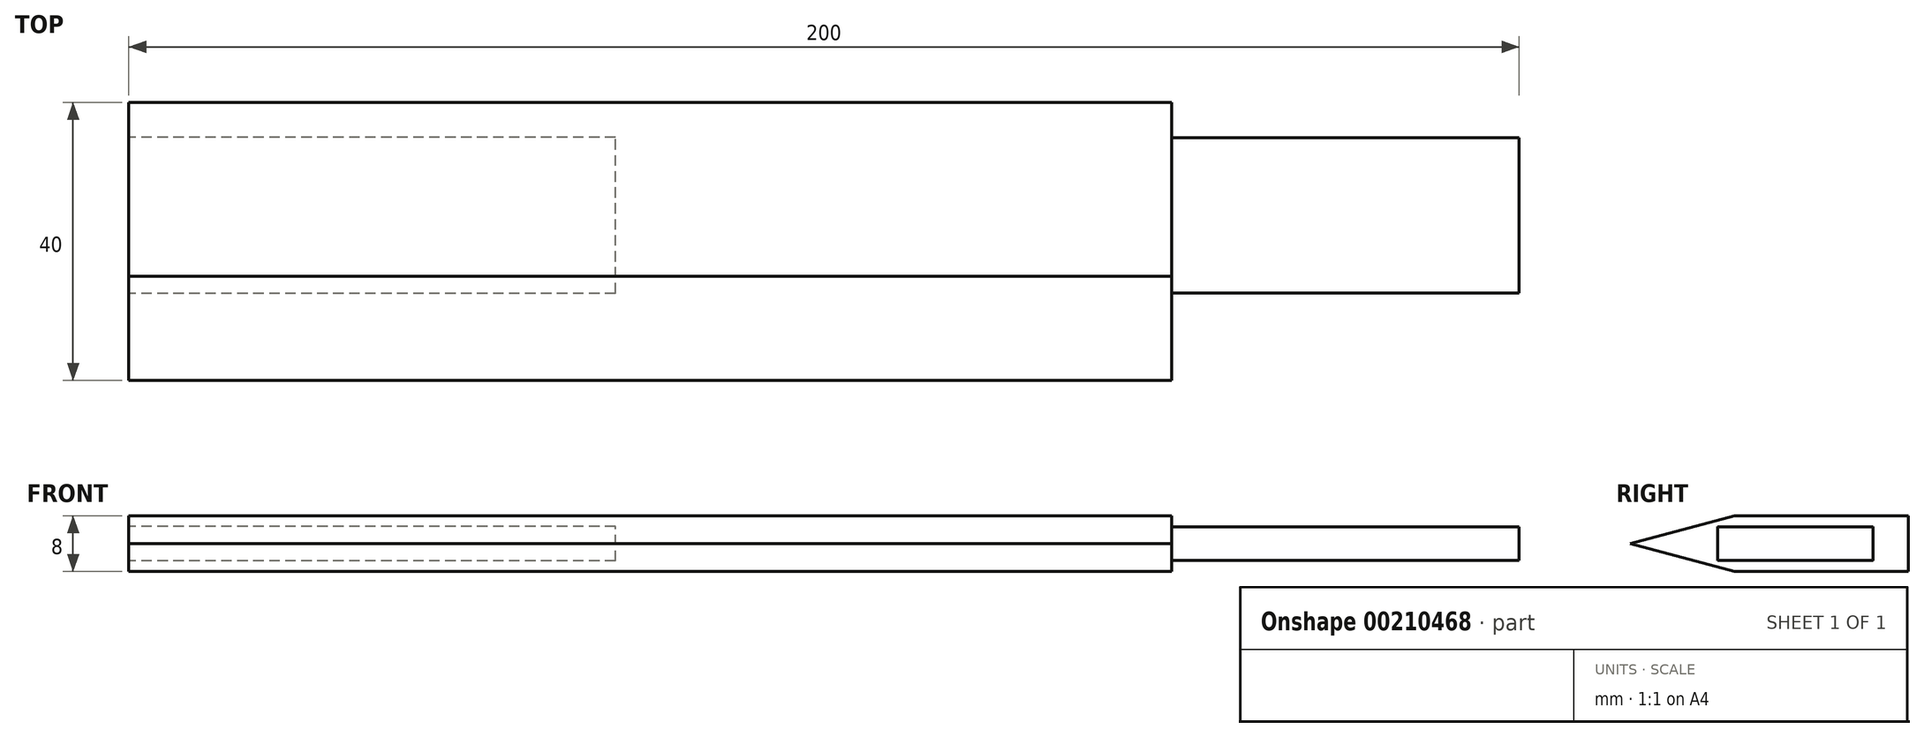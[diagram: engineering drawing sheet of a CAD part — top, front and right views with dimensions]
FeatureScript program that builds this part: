
annotation { "Feature Type Name" : "Feature", "Feature Type Description" : "" }
export const myFeature = defineFeature(function(context is Context, id is Id, definition is map)
    precondition{}
    {
        {
            var Q0;
            Q0=qCreatedBy(makeId("Top.planeOp"),FACE);
            var sketch = newSketch(context, id + "F0", { "sketchPlane" : qUnion([Q0])});
            skLineSegment(sketch, "E0.bottom", {"start": v(0, 0) * mm, "end": v(-150, 0) * mm});
            skLineSegment(sketch, "E0.top", {"start": v(0, 40) * mm, "end": v(-150, 40) * mm});
            skLineSegment(sketch, "E0.left", {"start": v(0, 0) * mm, "end": v(0, 40) * mm});
            skLineSegment(sketch, "E0.right", {"start": v(-150, 0) * mm, "end": v(-150, 40) * mm});
            skSolve(sketch);
        }
        {
            var Q0;
            Q0=makeQuery(id+"F0.imprint","IMPRINT",FACE,{"disambiguationData":[TD([[makeQuery(id+"F0.imprint","IMPRINT",EDGE,{"derivedFrom":sQuery(id+"F0.wireOp",EDGE,"E0.bottom")}),-1.0]])]});
            extrude(context, id + "F1", {"entities" : qUnion([Q0]), "depth" : 8 * mm});
        }
        {
            var Q0;
            Q0=makeQuery(id+"F1.opExtrude","CAP_EDGE",EDGE,{"disambiguationData":[OSD([sQuery(id+"F0.wireOp",EDGE,"E0.bottom")])],"isStart":false});
            var Q1;
            Q1=makeQuery(id+"F1.opExtrude","CAP_EDGE",EDGE,{"disambiguationData":[OSD([sQuery(id+"F0.wireOp",EDGE,"E0.bottom")])],"isStart":true});
            chamfer(context, id + "F2", {"entities" : qUnion([Q0, Q1]), "chamferType" : ChamferType.TWO_OFFSETS, "width1" : 4 * mm, "oppositeDirection" : false, "width2" : 15 * mm, "tangentPropagation" : true});
        }
        {
            var Q0;
            Q0=makeQuery(id+"F1.opExtrude","SWEPT_FACE",FACE,{"disambiguationData":[OSD([sQuery(id+"F0.wireOp",EDGE,"E0.right")])]});
            var sketch = newSketch(context, id + "F3", { "sketchPlane" : qUnion([Q0])});
            skLineSegment(sketch, "E1", {"start": v(0, 4) * mm, "end": v(-12.5, 4) * mm});
            skLineSegment(sketch, "E2", {"start": v(-12.5, 4) * mm, "end": v(-12.5, 6.5) * mm});
            skLineSegment(sketch, "E3", {"start": v(-12.5, 6.5) * mm, "end": v(-35, 6.5) * mm});
            skLineSegment(sketch, "E4", {"start": v(-35, 6.5) * mm, "end": v(-35, 1.5) * mm});
            skLineSegment(sketch, "E5", {"start": v(-35, 1.5) * mm, "end": v(-12.5, 1.5) * mm});
            skLineSegment(sketch, "E6", {"start": v(-12.5, 1.5) * mm, "end": v(-12.5, 4) * mm});
            skSolve(sketch);
        }
        {
            var Q0;
            Q0 = qSketchRegion(id + "F3", true);
            extrude(context, id + "F4", {"entities" : qUnion([Q0]), "operationType" : NewBodyOperationType.REMOVE, "oppositeDirection" : true, "depth" : 70 * mm});
        }
        {
            var Q0;
            Q0=makeQuery(id+"F1.opExtrude","SWEPT_FACE",FACE,{"disambiguationData":[OSD([sQuery(id+"F0.wireOp",EDGE,"E0.left")])]});
            var sketch = newSketch(context, id + "F5", { "sketchPlane" : qUnion([Q0])});
            skLineSegment(sketch, "E7", {"start": v(0, 4) * mm, "end": v(12.6, 4) * mm});
            skLineSegment(sketch, "E8", {"start": v(12.6, 4) * mm, "end": v(12.6, 6.4) * mm});
            skLineSegment(sketch, "E9", {"start": v(12.6, 6.4) * mm, "end": v(34.9, 6.4) * mm});
            skLineSegment(sketch, "E10", {"start": v(34.9, 6.4) * mm, "end": v(34.9, 1.6) * mm});
            skLineSegment(sketch, "E11", {"start": v(34.9, 1.6) * mm, "end": v(12.6, 1.6) * mm});
            skLineSegment(sketch, "E12", {"start": v(12.6, 1.6) * mm, "end": v(12.6, 4) * mm});
            skSolve(sketch);
        }
        {
            var Q0;
            Q0 = qSketchRegion(id + "F5", true);
            extrude(context, id + "F6", {"entities" : qUnion([Q0]), "operationType" : NewBodyOperationType.ADD, "depth" : 50 * mm});
        }
    });
